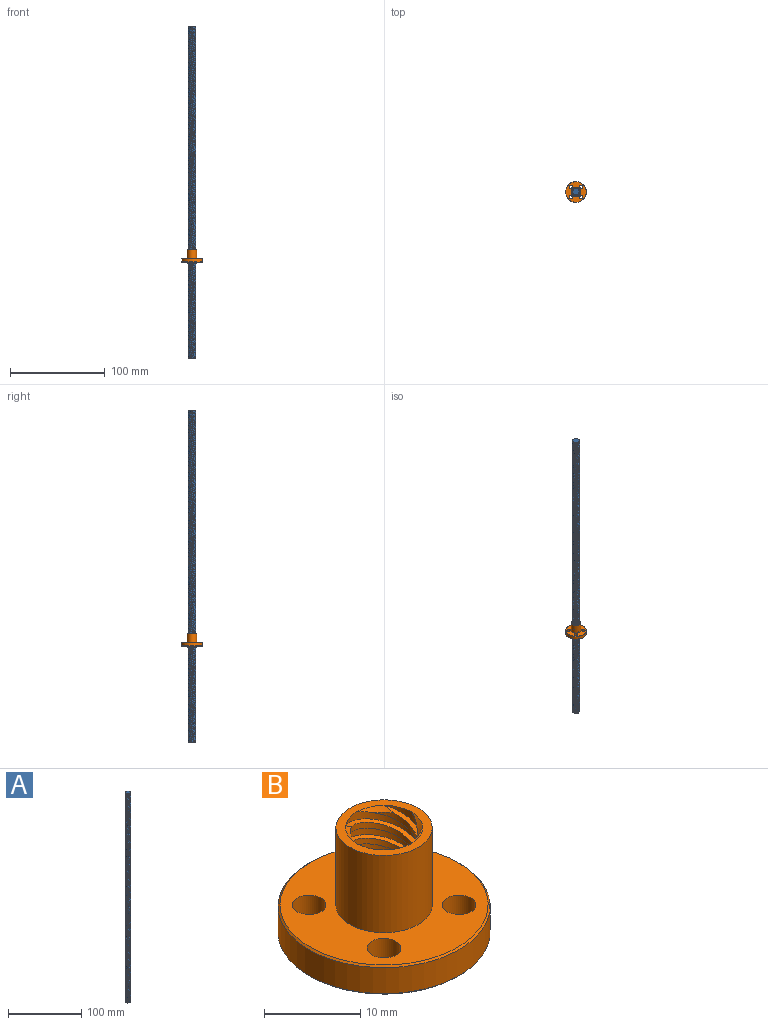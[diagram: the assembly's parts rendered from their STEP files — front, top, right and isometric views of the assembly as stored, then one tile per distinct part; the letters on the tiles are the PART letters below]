
ASSEMBLY  parts=2 mates=1
PART A: 26 faces, bbox 2424.7x2424.7x675.6 mm
  f0: cone r=4mm half-angle=45deg, axis (0,0,1), area 2.4mm2, adj f3,f18,f19,f23
  f1: cylinder r=4mm len=349mm, axis (0,0,-1), area 1095.6mm2, adj f5,f6,f8,f9
  f2: cone r=3.5mm half-angle=45deg, axis (0,0,-1), area 2.3mm2, adj f3,f19,f20,f23
  f3: bspline ~351.13x8mm, area 561.2mm2, adj f0,f2,f4,f19
  f4: cylinder r=3.5mm len=350mm, axis (0,0,1), area -492.9mm2, adj f3,f5,f18,f20
  f5: bspline ~1216.84x675.61mm, area 561.4mm2, adj f1,f4,f6,f8
  f6: cone r=4mm half-angle=45deg, axis (0,0,1), area 2.4mm2, adj f1,f5,f9,f18
  f7: cylinder r=4mm len=349mm, axis (0,0,-1), area 1095.6mm2, adj f11,f12,f14,f15
  f8: cone r=3.5mm half-angle=45deg, axis (0,0,-1), area 2.3mm2, adj f1,f5,f9,f20
  f9: bspline ~351.13x8mm, area 561.2mm2, adj f1,f6,f8,f10
  f10: cylinder r=3.5mm len=350mm, axis (0,0,1), area -492.9mm2, adj f9,f11,f18,f20
  f11: bspline ~1216.84x675.61mm, area 561.4mm2, adj f7,f10,f12,f14
  f12: cone r=4mm half-angle=45deg, axis (0,0,1), area 2.4mm2, adj f7,f11,f15,f18
  f13: cylinder r=4mm len=349mm, axis (0,0,-1), area 1095.6mm2, adj f17,f22,f24,f25
  f14: cone r=3.5mm half-angle=45deg, axis (0,0,-1), area 2.3mm2, adj f7,f11,f15,f20
  f15: bspline ~351.13x8mm, area 561.2mm2, adj f7,f12,f14,f16
  f16: cylinder r=3.5mm len=350mm, axis (0,0,1), area -492.9mm2, adj f15,f17,f18,f20
  f17: bspline ~1216.84x675.61mm, area 561.4mm2, adj f13,f16,f24,f25
  f18: plane 7x7mm, normal (0,0,-1), area 38.5mm2, adj f0,f4,f6,f10,f12,f16,f21,f25
  f19: cylinder r=4mm len=349mm, axis (0,0,-1), area 1095.6mm2, adj f0,f2,f3,f23
  f20: plane 7x7mm, normal (0,0,1), area 38.5mm2, adj f2,f4,f8,f10,f14,f16,f21,f24
  f21: cylinder r=3.5mm len=350mm, axis (0,0,1), area -492.9mm2, adj f18,f20,f22,f23
  f22: bspline ~351.13x8mm, area 561.2mm2, adj f13,f21,f24,f25
  f23: bspline ~1216.84x675.61mm, area 561.4mm2, adj f0,f2,f19,f21
  f24: cone r=3.5mm half-angle=45deg, axis (0,0,-1), area 2.3mm2, adj f13,f17,f20,f22
  f25: cone r=4mm half-angle=45deg, axis (0,0,1), area 2.4mm2, adj f13,f17,f18,f22
PART B: 37 faces, bbox 22x22x16.4 mm
  f0: cylinder r=1.75mm len=3.7mm, axis (0,0,-1), area 40.7mm2, adj f5,f6
  f1: cylinder r=1.75mm len=3.7mm, axis (0,0,-1), area 40.7mm2, adj f5,f6
  f2: cylinder r=1.75mm len=3.7mm, axis (0,0,-1), area 40.7mm2, adj f5,f6
  f3: cylinder r=1.75mm len=3.7mm, axis (0,0,-1), area 40.7mm2, adj f5,f6
  f4: cylinder r=11mm len=22mm, axis (0,0,-1), area 228.1mm2, adj f27,f28
  f5: plane 21.6x21.6mm, normal (0,0,1), area 249.4mm2, adj f0,f1,f2,f3,f9,f28
  f6: plane 21.6x21.6mm, normal (0,0,-1), area 249.4mm2, adj f0,f1,f2,f3,f8,f27
  f7: plane 10x10mm, normal (0,0,-1), area 28.3mm2, adj f8,f11,f15,f19,f23,f29,f30,f31
  f8: cylinder r=5mm len=10mm, axis (0,0,-1), area 47.1mm2, adj f6,f7
  f9: cylinder r=5mm len=10mm, axis (0,0,-1), area 307.9mm2, adj f5,f10
  f10: plane 10x10mm, normal (0,0,1), area 28.3mm2, adj f9,f11,f15,f19,f23,f33,f34,f35
  f11: cylinder r=4mm len=15mm, axis (0,0,-1), area 47.1mm2, adj f7,f10,f14,f16
  f12: bspline ~16.13x8mm, area 23.3mm2, adj f13,f23,f30,f36
  f13: cylinder r=3.5mm len=14mm, axis (0,0,1), area 28.2mm2, adj f12,f14,f30,f36
  f14: bspline ~16.4x9mm, area 23.3mm2, adj f11,f13,f30,f36
  f15: cylinder r=4mm len=15mm, axis (0,0,-1), area 47.1mm2, adj f7,f10,f18,f20
  f16: bspline ~16.13x8mm, area 23.3mm2, adj f11,f17,f29,f35
  f17: cylinder r=3.5mm len=14mm, axis (0,0,1), area 28.2mm2, adj f16,f18,f29,f35
  f18: bspline ~16.4x9mm, area 23.3mm2, adj f15,f17,f29,f35
  f19: cylinder r=4mm len=15mm, axis (0,0,-1), area 47.1mm2, adj f7,f10,f22,f25
  f20: bspline ~16.13x8mm, area 23.3mm2, adj f15,f21,f32,f34
  f21: cylinder r=3.5mm len=14mm, axis (0,0,1), area 28.2mm2, adj f20,f22,f32,f34
  f22: bspline ~16.4x9mm, area 23.3mm2, adj f19,f21,f32,f34
  f23: cylinder r=4mm len=15mm, axis (0,0,-1), area 47.1mm2, adj f7,f10,f12,f26
  f24: cylinder r=3.5mm len=14mm, axis (0,0,1), area 28.2mm2, adj f25,f26,f31,f33
  f25: bspline ~16.13x8mm, area 23.3mm2, adj f19,f24,f31,f33
  f26: bspline ~16.4x9mm, area 23.3mm2, adj f23,f24,f31,f33
  f27: cone r=11mm half-angle=45deg, axis (0,0,1), area 19.4mm2, adj f4,f6
  f28: cone r=10.8mm half-angle=45deg, axis (0,0,-1), area 19.4mm2, adj f4,f5
  f29: cone r=4mm half-angle=45deg, axis (0,0,-1), area 1.8mm2, adj f7,f16,f17,f18
  f30: cone r=4mm half-angle=45deg, axis (0,0,-1), area 1.8mm2, adj f7,f12,f13,f14
  f31: cone r=4mm half-angle=45deg, axis (0,0,-1), area 1.8mm2, adj f7,f24,f25,f26
  f32: cone r=4mm half-angle=45deg, axis (0,0,-1), area 1.8mm2, adj f7,f20,f21,f22
  f33: cone r=3.5mm half-angle=45deg, axis (0,0,1), area 1.8mm2, adj f10,f24,f25,f26
  f34: cone r=3.5mm half-angle=45deg, axis (0,0,1), area 1.8mm2, adj f10,f20,f21,f22
  f35: cone r=3.5mm half-angle=45deg, axis (0,0,1), area 1.8mm2, adj f10,f16,f17,f18
  f36: cone r=3.5mm half-angle=45deg, axis (0,0,1), area 1.8mm2, adj f10,f12,f13,f14
PLACE A rot(axis=(0,0,-1),21.3deg) t=(0,0,-93.03)mm
PLACE B at identity fixed
MATE cylindrical A.f0 <-> B.f11  axis (0,0,-1) through (0,0,6.97)mm
